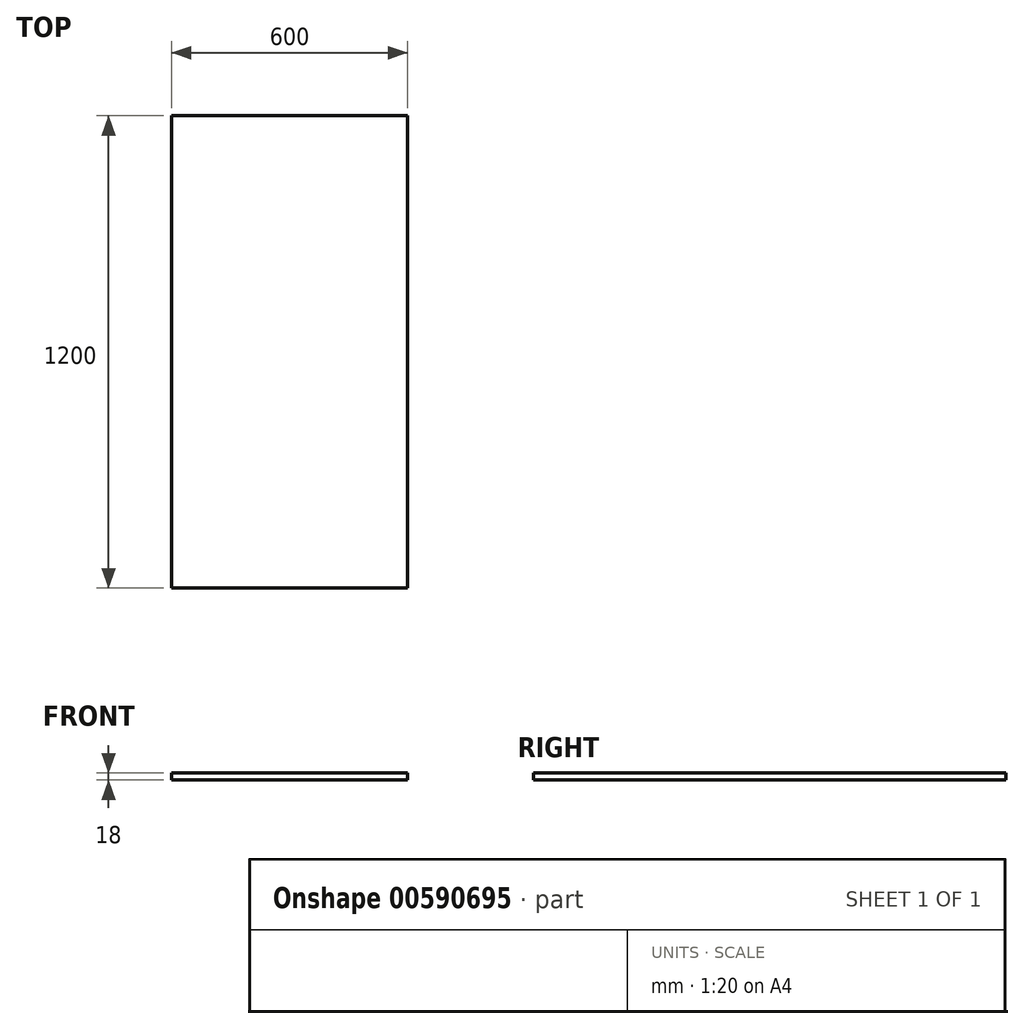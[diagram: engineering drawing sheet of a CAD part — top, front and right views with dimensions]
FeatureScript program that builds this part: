
annotation { "Feature Type Name" : "Feature", "Feature Type Description" : "" }
export const myFeature = defineFeature(function(context is Context, id is Id, definition is map)
    precondition{}
    {
        {
            assignVariable(context, id + "F0", {"name" : "longueur", "anyValue" : 1200});
        }
        {
            var Q0;
            Q0=qCreatedBy(makeId("Front.planeOp"),FACE);
            var sketch = newSketch(context, id + "F1", { "sketchPlane" : qUnion([Q0])});
            skLineSegment(sketch, "E0.bottom", {"start": v(-300, 9) * mm, "end": v(300, 9) * mm});
            skLineSegment(sketch, "E0.top", {"start": v(-300, -9) * mm, "end": v(300, -9) * mm});
            skLineSegment(sketch, "E0.left", {"start": v(-300, 9) * mm, "end": v(-300, -9) * mm});
            skLineSegment(sketch, "E0.right", {"start": v(300, 9) * mm, "end": v(300, -9) * mm});
            skPoint(sketch, "E0.middle", {"position": v(0, 0) * mm});
            skSolve(sketch);
        }
        {
            var Q0;
            Q0 = qSketchRegion(id + "F1", true);
            extrude(context, id + "F2", {"entities" : qUnion([Q0]), "endBound" : BoundingType.SYMMETRIC, "depth" : (getVariable(context, 'longueur')) * mm, "offsetDistance" : 25 * mm});
        }
    });
